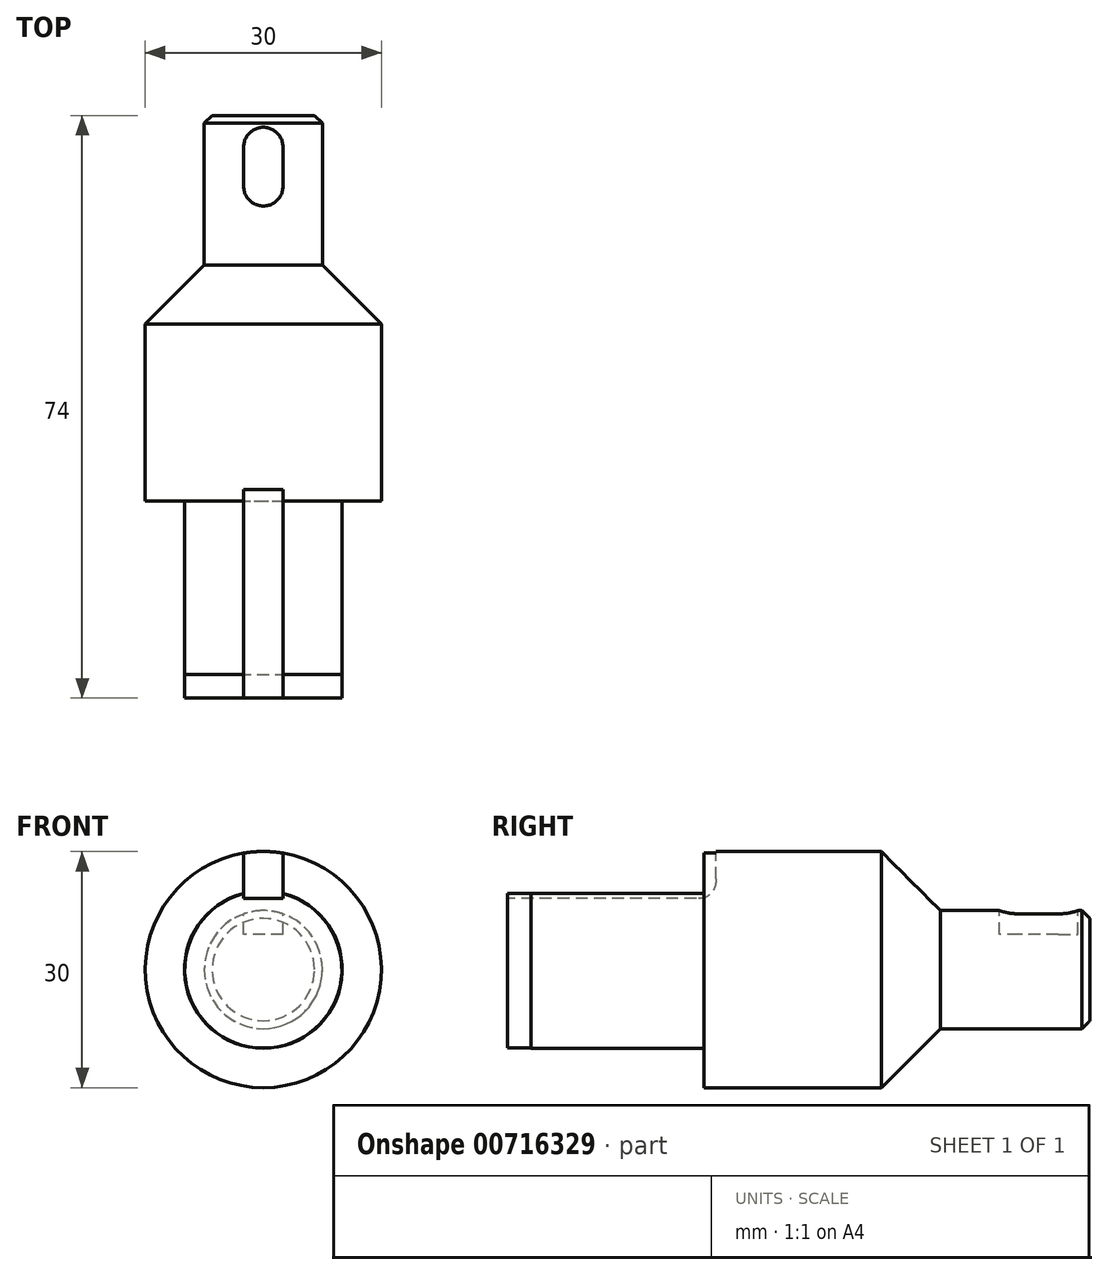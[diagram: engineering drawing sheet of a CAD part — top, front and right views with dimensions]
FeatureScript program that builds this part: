
annotation { "Feature Type Name" : "Feature", "Feature Type Description" : "" }
export const myFeature = defineFeature(function(context is Context, id is Id, definition is map)
    precondition{}
    {
        {
            var Q0;
            Q0=qCreatedBy(makeId("Front.planeOp"),FACE);
            var sketch = newSketch(context, id + "F0", { "sketchPlane" : qUnion([Q0])});
            skCircle(sketch, "E0", {"center": v(0, 0) * mm, "radius": 15 * mm});
            skSolve(sketch);
        }
        {
            var Q0;
            Q0 = qSketchRegion(id + "F0", true);
            extrude(context, id + "F1", {"entities" : qUnion([Q0]), "depth" : 74 * mm, "offsetDistance" : 25 * mm});
        }
        {
            var Q0;
            Q0=makeQuery(id+"F1.opExtrude","CAP_FACE",FACE,{"disambiguationData":[OSD([sQuery(id+"F0.wireOp",EDGE,"E0")])],"isStart":false});
            var sketch = newSketch(context, id + "F2", { "sketchPlane" : qUnion([Q0])});
            skCircle(sketch, "E1", {"center": v(0, 0) * mm, "radius": 9.97 * mm});
            skCircle(sketch, "E2", {"center": v(0, 0) * mm, "radius": 15 * mm});
            skSolve(sketch);
        }
        {
            var Q0;
            Q0 = qSketchRegion(id + "F2", true);
            extrude(context, id + "F3", {"entities" : qUnion([Q0]), "operationType" : NewBodyOperationType.REMOVE, "oppositeDirection" : true, "depth" : 3 * mm, "offsetDistance" : 25 * mm});
        }
        {
            var Q0;
            Q0=makeQuery(id+"F3.boolean.opBoolean","COPY",FACE,{"derivedFrom":makeQuery(id+"F3.opExtrude","CAP_FACE",FACE,{"disambiguationData":[OSD([sQuery(id+"F2.wireOp",EDGE,"E1"),sQuery(id+"F2.wireOp",EDGE,"E2")])],"isStart":false})});
            var sketch = newSketch(context, id + "F4", { "sketchPlane" : qUnion([Q0])});
            skCircle(sketch, "E3", {"center": v(0, 0) * mm, "radius": 10.02 * mm});
            skCircle(sketch, "E4", {"center": v(0, 0) * mm, "radius": 9.97 * mm});
            skCircle(sketch, "E5", {"center": v(0, 0) * mm, "radius": 15 * mm});
            skSolve(sketch);
        }
        {
            var Q0;
            Q0 = qSketchRegion(id + "F4", true);
            extrude(context, id + "F5", {"entities" : qUnion([Q0]), "operationType" : NewBodyOperationType.REMOVE, "oppositeDirection" : true, "depth" : 22 * mm, "offsetDistance" : 25 * mm});
        }
        {
            var Q0;
            Q0=qCreatedBy(makeId("Front.planeOp"),FACE);
            var sketch = newSketch(context, id + "F6", { "sketchPlane" : qUnion([Q0])});
            skCircle(sketch, "E6", {"center": v(0, 0) * mm, "radius": 7.5 * mm});
            skCircle(sketch, "E7", {"center": v(0, 0) * mm, "radius": 15 * mm});
            skSolve(sketch);
        }
        {
            var Q0;
            Q0 = qSketchRegion(id + "F6", true);
            extrude(context, id + "F7", {"entities" : qUnion([Q0]), "operationType" : NewBodyOperationType.REMOVE, "depth" : 19 * mm, "offsetDistance" : 25 * mm});
        }
        {
            var Q0;
            Q0=makeQuery(id+"F1.opExtrude","CAP_FACE",FACE,{"disambiguationData":[OSD([sQuery(id+"F0.wireOp",EDGE,"E0")])],"isStart":true});
            var Q1;
            Q1=makeQuery(id+"F3.boolean.opBoolean","COPY",EDGE,{"derivedFrom":makeQuery(id+"F3.opExtrude","CAP_EDGE",EDGE,{"disambiguationData":[OSD([sQuery(id+"F2.wireOp",EDGE,"E1")])],"isStart":true})});
            chamfer(context, id + "F8", {"entities" : qUnion([Q0, Q1]), "chamferType" : ChamferType.OFFSET_ANGLE, "width" : 1 * mm, "oppositeDirection" : false, "angle" : 45 * degree, "tangentPropagation" : true});
        }
        {
            var Q0;
            Q0=qCreatedBy(makeId("Right.planeOp"),FACE);
            var sketch = newSketch(context, id + "F9", { "sketchPlane" : qUnion([Q0])});
            skLineSegment(sketch, "E8", {"start": v(-19, 0) * mm, "end": v(-19, 7.5) * mm});
            skLineSegment(sketch, "E9", {"start": v(-26.5, 0) * mm, "end": v(-19, 0) * mm});
            skLineSegment(sketch, "E10", {"start": v(-19, 7.5) * mm, "end": v(-26.5, 15) * mm});
            skPoint(sketch, "E11.end.orphan", {"position": v(-49, 0) * mm});
            skLineSegment(sketch, "E12", {"start": v(-19, 7.5) * mm, "end": v(-19, 15) * mm});
            skLineSegment(sketch, "E13", {"start": v(-19, 15) * mm, "end": v(-26.5, 15) * mm});
            skSolve(sketch);
        }
        {
            var Q0;
            Q0 = qSketchRegion(id + "F9", true);
            var Q1;
            Q1=sQuery(id+"F9.wireOp",EDGE,"E9");
            revolve(context, id + "F10", {"operationType" : NewBodyOperationType.REMOVE, "surfaceOperationType" : NewSurfaceOperationType.NEW, "entities" : qUnion([Q0]), "axis" : qUnion([Q1]), "revolveType" : RevolveType.FULL, "oppositeDirection" : true});
        }
        {
            var Q0;
            Q0=makeQuery(id+"F1.opExtrude","CAP_FACE",FACE,{"disambiguationData":[OSD([sQuery(id+"F0.wireOp",EDGE,"E0")])],"isStart":false});
            var sketch = newSketch(context, id + "F11", { "sketchPlane" : qUnion([Q0])});
            skLineSegment(sketch, "E14", {"start": v(0, 9.02) * mm, "end": v(0, 10.02) * mm});
            skLineSegment(sketch, "E15", {"start": v(-2.5, 10.02) * mm, "end": v(-2.5, 9.02) * mm});
            skLineSegment(sketch, "E16", {"start": v(2.5, 9.02) * mm, "end": v(2.5, 10.02) * mm});
            skLineSegment(sketch, "E17", {"start": v(2.5, 10.02) * mm, "end": v(2.5, 9.02) * mm});
            skLineSegment(sketch, "E18", {"start": v(2.5, 9.02) * mm, "end": v(-2.5, 9.02) * mm});
            skPoint(sketch, "E19.start.orphan", {"position": v(-2.5, 0) * mm});
            skLineSegment(sketch, "E20", {"start": v(-2.5, 10.02) * mm, "end": v(-2.5, 14.8) * mm});
            skLineSegment(sketch, "E21", {"start": v(2.5, 14.8) * mm, "end": v(2.5, 10.02) * mm});
            skPoint(sketch, "E22.center.orphan", {"position": v(0, 0) * mm});
            skArc(sketch, "E23", {"start": v(2.5, 14.8) * mm, "mid": v(0, 15) * mm, "end": v(-2.5, 14.8) * mm});
            skSolve(sketch);
        }
        {
            var Q0;
            Q0 = qSketchRegion(id + "F11", true);
            extrude(context, id + "F12", {"entities" : qUnion([Q0]), "operationType" : NewBodyOperationType.REMOVE, "oppositeDirection" : true, "depth" : 26.5 * mm, "offsetDistance" : 25 * mm});
        }
        {
            var Q0;
            Q0=makeQuery(id+"F12.boolean.opBoolean","COPY",EDGE,{"derivedFrom":makeQuery(id+"F12.opExtrude","CAP_EDGE",EDGE,{"disambiguationData":[OSD([sQuery(id+"F11.wireOp",EDGE,"E18")])],"isStart":false})});
            fillet(context, id + "F13", {"entities" : qUnion([Q0]), "radius" : 2.5 * mm, "tangentPropagation" : true, "rho" : 0.5, "crossSection" : FilletCrossSection.CONIC, "allowEdgeOverflow" : false});
        }
        {
            var Q0;
            Q0=qCreatedBy(makeId("Top.planeOp"),FACE);
            cPlane(context, id + "F14", {"entities" : qUnion([Q0]), "cplaneType" : CPlaneType.OFFSET, "offset" : 7.5 * mm, "width" : 150 * mm, "height" : 150 * mm});
        }
        {
            var Q0;
            Q0=qCreatedBy(id+"F14.planeOp",FACE);
            var sketch = newSketch(context, id + "F15", { "sketchPlane" : qUnion([Q0])});
            skLineSegment(sketch, "E24.right", {"start": v(2.5, -4) * mm, "end": v(2.5, -9) * mm});
            skLineSegment(sketch, "E25.MirrorCS", {"start": v(-2.5, -4) * mm, "end": v(-2.5, -9) * mm});
            skLineSegment(sketch, "E26", {"start": v(0, -1.5) * mm, "end": v(0, -1.5) * mm});
            skLineSegment(sketch, "E27", {"start": v(0, -11.5) * mm, "end": v(0, -11.5) * mm});
            skPoint(sketch, "E28.visualSharp", {"position": v(-2.5, -1.5) * mm});
            skArc(sketch, "E28.filletArc", {"start": v(0, -1.5) * mm, "mid": v(-1.77, -2.23) * mm, "end": v(-2.5, -4) * mm});
            skPoint(sketch, "E29.visualSharp", {"position": v(2.5, -1.5) * mm});
            skArc(sketch, "E29.filletArc", {"start": v(2.5, -4) * mm, "mid": v(1.77, -2.23) * mm, "end": v(0, -1.5) * mm});
            skPoint(sketch, "E30.visualSharp", {"position": v(-2.5, -11.5) * mm});
            skArc(sketch, "E30.filletArc", {"start": v(-2.5, -9) * mm, "mid": v(-1.77, -10.77) * mm, "end": v(0, -11.5) * mm});
            skPoint(sketch, "E31.visualSharp", {"position": v(2.5, -11.5) * mm});
            skArc(sketch, "E31.filletArc", {"start": v(0, -11.5) * mm, "mid": v(1.77, -10.77) * mm, "end": v(2.5, -9) * mm});
            skSolve(sketch);
        }
        {
            var Q0;
            Q0 = qSketchRegion(id + "F15", true);
            extrude(context, id + "F16", {"entities" : qUnion([Q0]), "operationType" : NewBodyOperationType.REMOVE, "oppositeDirection" : true, "depth" : 3 * mm, "offsetDistance" : 25 * mm});
        }
    });
